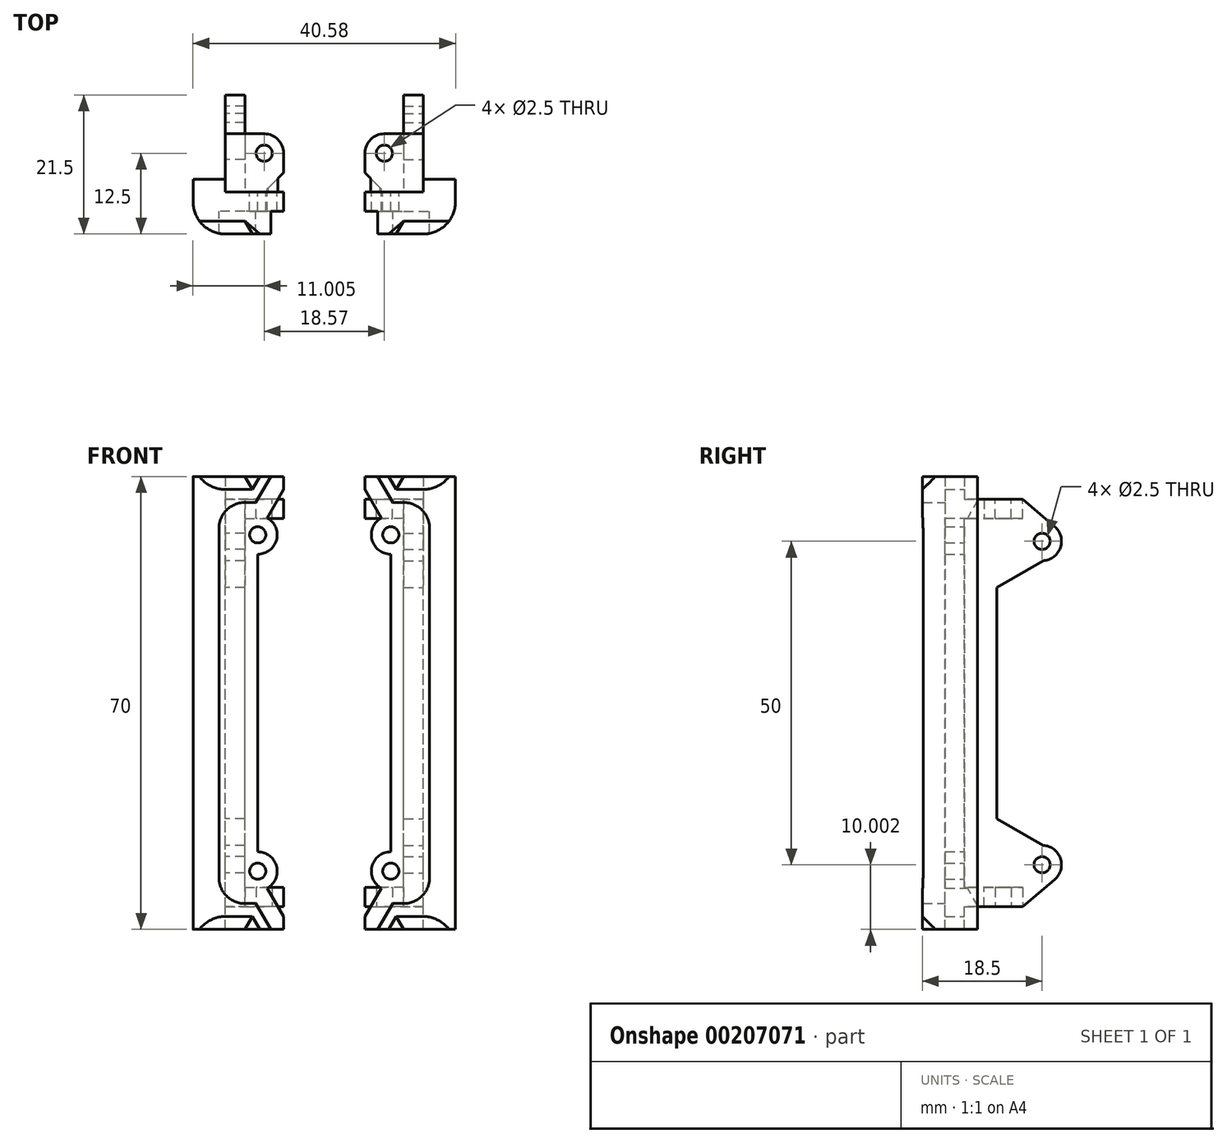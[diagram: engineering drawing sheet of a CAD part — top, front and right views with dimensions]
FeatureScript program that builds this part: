
annotation { "Feature Type Name" : "Feature", "Feature Type Description" : "" }
export const myFeature = defineFeature(function(context is Context, id is Id, definition is map)
    precondition{}
    {
        {
            var Q0;
            Q0=qCreatedBy(makeId("Front.planeOp"),FACE);
            var sketch = newSketch(context, id + "F0", { "sketchPlane" : qUnion([Q0])});
            skLineSegment(sketch, "E0", {"start": v(8.29, 4.8) * mm, "end": v(20.29, 4.8) * mm});
            skLineSegment(sketch, "E1", {"start": v(20.29, 4.8) * mm, "end": v(20.29, 13.8) * mm});
            skLineSegment(sketch, "E2", {"start": v(20.29, 13.8) * mm, "end": v(16.29, 13.8) * mm});
            skLineSegment(sketch, "E3", {"start": v(10.6, 4.8) * mm, "end": v(10.6, 8.8) * mm, "construction": true});
            skLineSegment(sketch, "E4", {"start": v(8.29, 4.8) * mm, "end": v(10.6, 8.8) * mm});
            skLineSegment(sketch, "E5", {"start": v(10.6, 8.8) * mm, "end": v(12.29, 8.8) * mm});
            skLineSegment(sketch, "E6", {"start": v(16.29, 12.8) * mm, "end": v(16.29, 13.8) * mm});
            skArc(sketch, "E7.filletArc", {"start": v(12.29, 8.8) * mm, "mid": v(15.11, 9.97) * mm, "end": v(16.29, 12.8) * mm});
            skLineSegment(sketch, "E8", {"start": v(9.19, 6.36) * mm, "end": v(12.65, 4.36) * mm, "construction": true});
            skLineSegment(sketch, "E9", {"start": v(12.29, 4.8) * mm, "end": v(15.79, 4.8) * mm});
            skLineSegment(sketch, "E10", {"start": v(20.29, 9.3) * mm, "end": v(20.29, 13.8) * mm});
            skPoint(sketch, "E11.visualSharp", {"position": v(20.29, 4.8) * mm});
            skLineSegment(sketch, "E12", {"start": v(8.29, 4.8) * mm, "end": v(6.29, 4.8) * mm});
            skLineSegment(sketch, "E13", {"start": v(6.29, 4.8) * mm, "end": v(6.29, 6.8) * mm});
            skLineSegment(sketch, "E14", {"start": v(6.29, 6.8) * mm, "end": v(8.6, 10.8) * mm});
            skLineSegment(sketch, "E15", {"start": v(16.29, 13.8) * mm, "end": v(14.29, 13.8) * mm});
            skLineSegment(sketch, "E16", {"start": v(14.29, 13.8) * mm, "end": v(10.29, 13.8) * mm, "construction": true});
            skCircle(sketch, "E17", {"center": v(10.29, 13.8) * mm, "radius": 1.25 * mm});
            skCircle(sketch, "E18", {"center": v(10.29, 13.8) * mm, "radius": 3 * mm});
            skLineSegment(sketch, "E19", {"start": v(8.6, 10.8) * mm, "end": v(8.82, 11.19) * mm});
            skLineSegment(sketch, "E20", {"start": v(10.29, 13.8) * mm, "end": v(10.29, 16.8) * mm, "construction": true});
            skLineSegment(sketch, "E21", {"start": v(10.29, 16.8) * mm, "end": v(20.29, 16.8) * mm});
            skLineSegment(sketch, "E22", {"start": v(20.29, 16.8) * mm, "end": v(20.29, 13.8) * mm});
            skLineSegment(sketch, "E23", {"start": v(20.29, 13.8) * mm, "end": v(20.29, 16.8) * mm});
            skLineSegment(sketch, "E24", {"start": v(16.29, 13.8) * mm, "end": v(16.29, 16.8) * mm});
            skLineSegment(sketch, "E25", {"start": v(12.29, 8.8) * mm, "end": v(12.29, 4.8) * mm});
            skSolve(sketch);
        }
        {
            var Q0;
            {var subQ0=sQuery(id+"F0.wireOp",EDGE,"E4");Q0=makeQuery(id+"F0.imprint","IMPRINT",FACE,{"disambiguationData":[TD([[makeQuery(id+"F0.imprint","IMPRINT",EDGE,{"derivedFrom":subQ0}),-1.0]])]});}
            var Q1;
            {var subQ0=sQuery(id+"F0.wireOp",EDGE,"E1");Q1=makeQuery(id+"F0.imprint","IMPRINT",FACE,{"disambiguationData":[TD([[makeQuery(id+"F0.imprint","IMPRINT",EDGE,{"derivedFrom":subQ0}),1.0]])]});}
            var Q2;
            Q2=makeQuery(id+"F0.imprint","IMPRINT",FACE,{"disambiguationData":[TD([[makeQuery(id+"F0.imprint","IMPRINT",EDGE,{"derivedFrom":sQuery(id+"F0.wireOp",EDGE,"E2")}),1.0]])]});
            var Q3;
            Q3=makeQuery(id+"F0.imprint","IMPRINT",FACE,{"disambiguationData":[TD([[makeQuery(id+"F0.imprint","IMPRINT",EDGE,{"derivedFrom":sQuery(id+"F0.wireOp",EDGE,"E2")}),-1.0]])]});
            extrude(context, id + "F1", {"entities" : qUnion([Q0, Q1, Q2, Q3]), "depth" : 6.5 * mm});
        }
        {
            var Q0;
            Q0 = qSketchRegion(id + "F0", true);
            extrude(context, id + "F2", {"entities" : qUnion([Q0]), "operationType" : NewBodyOperationType.ADD, "depth" : 3 * mm});
        }
        {
            var Q0;
            {var subQ0=sQuery(id+"F0.wireOp",EDGE,"E21");Q0=makeQuery(id+"F2.boolean.opBoolean","MERGE",FACE,{"derivedFrom":[makeQuery(id+"F1.opExtrude","SWEPT_FACE",FACE,{"disambiguationData":[OSD([subQ0])]}),makeQuery(id+"F2.opExtrude","SWEPT_FACE",FACE,{"disambiguationData":[OSD([subQ0])]})]});}
            var sketch = newSketch(context, id + "F3", { "sketchPlane" : qUnion([Q0])});
            skLineSegment(sketch, "E26", {"start": v(20.29, 0) * mm, "end": v(12.29, 0) * mm});
            skLineSegment(sketch, "E27", {"start": v(20.29, 0) * mm, "end": v(20.29, 2) * mm});
            skLineSegment(sketch, "E28", {"start": v(20.29, 2) * mm, "end": v(15.29, 2) * mm});
            skLineSegment(sketch, "E29", {"start": v(15.29, 2) * mm, "end": v(15.29, 5) * mm});
            skLineSegment(sketch, "E30", {"start": v(15.29, 5) * mm, "end": v(12.29, 5) * mm});
            skLineSegment(sketch, "E31", {"start": v(12.29, 5) * mm, "end": v(12.29, 0) * mm});
            skLineSegment(sketch, "E32", {"start": v(12.29, 0) * mm, "end": v(12.29, -3) * mm});
            skLineSegment(sketch, "E33", {"start": v(12.29, -3) * mm, "end": v(16.29, -3) * mm});
            skLineSegment(sketch, "E34", {"start": v(16.29, -3) * mm, "end": v(16.29, -6.5) * mm});
            skLineSegment(sketch, "E35", {"start": v(15.29, 2) * mm, "end": v(15.29, 0) * mm});
            skLineSegment(sketch, "E36", {"start": v(16.29, -6.5) * mm, "end": v(20.29, -6.5) * mm});
            skLineSegment(sketch, "E37", {"start": v(20.29, -6.5) * mm, "end": v(20.29, 0) * mm});
            skSolve(sketch);
        }
        {
            var Q0;
            Q0=makeQuery(id+"F3.imprint","IMPRINT",FACE,{"disambiguationData":[TD([[makeQuery(id+"F3.imprint","IMPRINT",EDGE,{"derivedFrom":sQuery(id+"F3.wireOp",EDGE,"E29")}),1.0]])]});
            extrude(context, id + "F4", {"entities" : qUnion([Q0]), "operationType" : NewBodyOperationType.ADD, "oppositeDirection" : true, "depth" : 8.5 * mm});
        }
        {
            var Q0;
            {var subQ0=sQuery(id+"F3.wireOp",EDGE,"E27");Q0=makeQuery(id+"F3.imprint","IMPRINT",FACE,{"disambiguationData":[TD([[makeQuery(id+"F3.imprint","IMPRINT",EDGE,{"derivedFrom":subQ0}),1.0]])]});}
            extrude(context, id + "F5", {"entities" : qUnion([Q0]), "operationType" : NewBodyOperationType.ADD, "oppositeDirection" : true, "depth" : 12 * mm});
        }
        {
            var Q0;
            Q0=makeQuery(id+"F1.opExtrude","CAP_FACE",FACE,{"disambiguationData":[OSD([sQuery(id+"F0.wireOp",EDGE,"E0"),sQuery(id+"F0.wireOp",EDGE,"E1"),sQuery(id+"F0.wireOp",EDGE,"E4"),sQuery(id+"F0.wireOp",EDGE,"E5"),sQuery(id+"F0.wireOp",EDGE,"E6"),sQuery(id+"F0.wireOp",EDGE,"E7.filletArc"),sQuery(id+"F0.wireOp",EDGE,"E9"),sQuery(id+"F0.wireOp",EDGE,"E10"),sQuery(id+"F0.wireOp",EDGE,"E21"),sQuery(id+"F0.wireOp",EDGE,"E23"),sQuery(id+"F0.wireOp",EDGE,"E24")])],"isStart":false});
            var sketch = newSketch(context, id + "F6", { "sketchPlane" : qUnion([Q0])});
            skLineSegment(sketch, "E38", {"start": v(8.29, 4.8) * mm, "end": v(12.29, 4.8) * mm});
            skLineSegment(sketch, "E39", {"start": v(8.29, 4.8) * mm, "end": v(9.79, 7.4) * mm});
            skLineSegment(sketch, "E40", {"start": v(9.79, 7.4) * mm, "end": v(13.79, 7.4) * mm});
            skLineSegment(sketch, "E41", {"start": v(13.79, 7.4) * mm, "end": v(12.29, 4.8) * mm});
            skSolve(sketch);
        }
        {
            var Q0;
            Q0=makeQuery(id+"F1.opExtrude","CAP_EDGE",EDGE,{"disambiguationData":[OSD([sQuery(id+"F0.wireOp",EDGE,"E0"),sQuery(id+"F0.wireOp",EDGE,"E9")])],"isStart":false});
            chamfer(context, id + "F7", {"entities" : qUnion([Q0]), "width" : 2 * mm, "tangentPropagation" : true});
        }
        {
            var Q0;
            Q0=makeQuery(id+"F6.imprint","IMPRINT",FACE,{"disambiguationData":[TD([[makeQuery(id+"F6.imprint","IMPRINT",EDGE,{"derivedFrom":sQuery(id+"F6.wireOp",EDGE,"E38")}),1.0]])]});
            extrude(context, id + "F8", {"entities" : qUnion([Q0]), "operationType" : NewBodyOperationType.ADD, "oppositeDirection" : true, "depth" : 3 * mm});
        }
        {
            var Q0;
            Q0=makeQuery(id+"F8.opExtrude","CAP_EDGE",EDGE,{"disambiguationData":[OSD([sQuery(id+"F6.wireOp",EDGE,"E41")])],"isStart":true});
            chamfer(context, id + "F9", {"entities" : qUnion([Q0]), "width" : 2 * mm, "tangentPropagation" : true});
        }
        {
            var Q0;
            Q0=makeQuery(id+"F4.opExtrude","CAP_FACE",FACE,{"disambiguationData":[OSD([sQuery(id+"F3.wireOp",EDGE,"E26"),sQuery(id+"F3.wireOp",EDGE,"E29"),sQuery(id+"F3.wireOp",EDGE,"E30"),sQuery(id+"F3.wireOp",EDGE,"E31"),sQuery(id+"F3.wireOp",EDGE,"E35")])],"isStart":false});
            var sketch = newSketch(context, id + "F10", { "sketchPlane" : qUnion([Q0])});
            skLineSegment(sketch, "E42", {"start": v(15.29, 0) * mm, "end": v(15.29, -6) * mm, "construction": true});
            skLineSegment(sketch, "E43", {"start": v(15.29, -6) * mm, "end": v(9.29, -6) * mm, "construction": true});
            skCircle(sketch, "E44", {"center": v(9.29, -6) * mm, "radius": 1.25 * mm});
            skCircle(sketch, "E45", {"center": v(9.29, -6) * mm, "radius": 3 * mm});
            skLineSegment(sketch, "E46", {"start": v(9.29, -6) * mm, "end": v(15.29, 0) * mm, "construction": true});
            skLineSegment(sketch, "E47", {"start": v(9.29, -6) * mm, "end": v(7.16, -3.88) * mm, "construction": true});
            skLineSegment(sketch, "E48", {"start": v(9.29, -6) * mm, "end": v(11.4, -8.12) * mm, "construction": true});
            skLineSegment(sketch, "E49", {"start": v(15.29, -5) * mm, "end": v(15.29, -9) * mm});
            skLineSegment(sketch, "E50", {"start": v(15.29, -9) * mm, "end": v(9.29, -9) * mm});
            skLineSegment(sketch, "E51", {"start": v(15.29, 0) * mm, "end": v(6.29, 0) * mm});
            skLineSegment(sketch, "E52", {"start": v(6.29, 0) * mm, "end": v(6.29, -6) * mm});
            skSolve(sketch);
        }
        {
            var Q0;
            Q0 = qSketchRegion(id + "F10", true);
            var Q1;
            Q1=makeQuery(id+"F10.imprint","IMPRINT",FACE,{"disambiguationData":[TD([[makeQuery(id+"F10.imprint","IMPRINT",EDGE,{"derivedFrom":sQuery(id+"F10.wireOp",EDGE,"E49")}),-1.0]])]});
            extrude(context, id + "F11", {"entities" : qUnion([Q0, Q1]), "operationType" : NewBodyOperationType.ADD, "oppositeDirection" : true, "depth" : 3 * mm});
        }
        {
            var Q0;
            Q0=makeQuery(id+"F11.opExtrude","SWEPT_EDGE",EDGE,{"disambiguationData":[OSD([sQuery(id+"F10.wireOp",EDGE,"E51"),sQuery(id+"F10.wireOp",EDGE,"E52")])]});
            chamfer(context, id + "F12", {"entities" : qUnion([Q0]), "width" : 3 * mm, "tangentPropagation" : true});
        }
        {
            var Q0;
            {var subQ0=sQuery(id+"F3.wireOp",EDGE,"E35");var subQ1=sQuery(id+"F3.wireOp",EDGE,"E26");var subQ2=sQuery(id+"F0.wireOp",EDGE,"E21");Q0=makeQuery(id+"F5.boolean.opBoolean","MERGE",FACE,{"derivedFrom":[makeQuery(id+"F4.boolean.opBoolean","MERGE",FACE,{"derivedFrom":[makeQuery(id+"F2.boolean.opBoolean","MERGE",FACE,{"derivedFrom":[makeQuery(id+"F1.opExtrude","SWEPT_FACE",FACE,{"disambiguationData":[OSD([subQ2])]}),makeQuery(id+"F2.opExtrude","SWEPT_FACE",FACE,{"disambiguationData":[OSD([subQ2])]})]}),makeQuery(id+"F4.opExtrude","CAP_FACE",FACE,{"disambiguationData":[OSD([subQ1,sQuery(id+"F3.wireOp",EDGE,"E29"),sQuery(id+"F3.wireOp",EDGE,"E30"),sQuery(id+"F3.wireOp",EDGE,"E31"),subQ0])],"isStart":true})]}),makeQuery(id+"F5.opExtrude","CAP_FACE",FACE,{"disambiguationData":[OSD([subQ1,sQuery(id+"F3.wireOp",EDGE,"E27"),sQuery(id+"F3.wireOp",EDGE,"E28"),subQ0])],"isStart":true})]});}
            extrude(context, id + "F13", {"entities" : qUnion([Q0]), "operationType" : NewBodyOperationType.ADD, "depth" : 23 * mm});
        }
        {
            var Q0;
            {var subQ0=sQuery(id+"F3.wireOp",EDGE,"E35");var subQ1=sQuery(id+"F3.wireOp",EDGE,"E29");Q0=makeQuery(id+"F13.boolean.opBoolean","MERGE",FACE,{"derivedFrom":[makeQuery(id+"F11.boolean.opBoolean","MERGE",FACE,{"derivedFrom":[makeQuery(id+"F4.opExtrude","SWEPT_FACE",FACE,{"disambiguationData":[OSD([subQ1,subQ0])]}),makeQuery(id+"F11.opExtrude","SWEPT_FACE",FACE,{"disambiguationData":[OSD([sQuery(id+"F10.wireOp",EDGE,"E49")])]})]}),makeQuery(id+"F13.opExtrude","SWEPT_FACE",FACE,{"disambiguationData":[OSD([subQ1,subQ0])]})]});}
            var sketch = newSketch(context, id + "F14", { "sketchPlane" : qUnion([Q0])});
            skLineSegment(sketch, "E53", {"start": v(5, 11.3) * mm, "end": v(5, 14.8) * mm});
            skCircle(sketch, "E54", {"center": v(12, 14.8) * mm, "radius": 1.25 * mm});
            skCircle(sketch, "E55", {"center": v(12, 14.8) * mm, "radius": 3 * mm});
            skLineSegment(sketch, "E56", {"start": v(12.15, 17.8) * mm, "end": v(5, 21.93) * mm});
            skLineSegment(sketch, "E57", {"start": v(5, 21.93) * mm, "end": v(5, 14.8) * mm});
            skLineSegment(sketch, "E58", {"start": v(12, 14.8) * mm, "end": v(5, 14.8) * mm, "construction": true});
            skLineSegment(sketch, "E59", {"start": v(9, 8.3) * mm, "end": v(13.95, 12.52) * mm});
            skSolve(sketch);
        }
        {
            var Q0;
            Q0=makeQuery(id+"F14.imprint","IMPRINT",FACE,{"disambiguationData":[TD([[makeQuery(id+"F14.imprint","IMPRINT",EDGE,{"derivedFrom":sQuery(id+"F14.wireOp",EDGE,"E53")}),-1.0]])]});
            var Q1;
            Q1=makeQuery(id+"F14.imprint","IMPRINT",FACE,{"disambiguationData":[TD([[makeQuery(id+"F14.imprint","IMPRINT",EDGE,{"derivedFrom":sQuery(id+"F14.wireOp",EDGE,"E54")}),-1.0]])]});
            var Q2;
            {var subQ0=sQuery(id+"F14.wireOp",EDGE,"E59");Q2=makeQuery(id+"F14.imprint","IMPRINT",FACE,{"disambiguationData":[TD([[makeQuery(id+"F14.imprint","IMPRINT",EDGE,{"derivedFrom":subQ0}),1.0]])]});}
            extrude(context, id + "F15", {"entities" : qUnion([Q0, Q1, Q2]), "operationType" : NewBodyOperationType.ADD, "oppositeDirection" : true, "depth" : 3 * mm});
        }
        {
            var Q0;
            Q0=makeQuery(id+"F1.opExtrude","SWEPT_BODY",BODY,{"disambiguationData":[OSD([sQuery(id+"F0.wireOp",EDGE,"E0"),sQuery(id+"F0.wireOp",EDGE,"E1"),sQuery(id+"F0.wireOp",EDGE,"E4"),sQuery(id+"F0.wireOp",EDGE,"E5"),sQuery(id+"F0.wireOp",EDGE,"E6"),sQuery(id+"F0.wireOp",EDGE,"E7.filletArc"),sQuery(id+"F0.wireOp",EDGE,"E9"),sQuery(id+"F0.wireOp",EDGE,"E10"),sQuery(id+"F0.wireOp",EDGE,"E21"),sQuery(id+"F0.wireOp",EDGE,"E23"),sQuery(id+"F0.wireOp",EDGE,"E24")])]});
            var Q1;
            Q1=makeQuery(id+"F13.opExtrude","CAP_FACE",FACE,{"disambiguationData":[OSD([sQuery(id+"F0.wireOp",EDGE,"E21"),sQuery(id+"F3.wireOp",EDGE,"E26"),sQuery(id+"F3.wireOp",EDGE,"E27"),sQuery(id+"F3.wireOp",EDGE,"E28"),sQuery(id+"F3.wireOp",EDGE,"E29"),sQuery(id+"F3.wireOp",EDGE,"E30"),sQuery(id+"F3.wireOp",EDGE,"E31"),sQuery(id+"F3.wireOp",EDGE,"E35")])],"isStart":false});
            mirror(context, id + "F16", {"operationType" : NewBodyOperationType.ADD, "entities" : qUnion([Q0]), "mirrorPlane" : qUnion([Q1])});
        }
        {
            var Q0;
            {var subQ0=sQuery(id+"F0.wireOp",EDGE,"E23");var subQ1=makeQuery(id+"F13.boolean.opBoolean","MERGE",EDGE,{"derivedFrom":[makeQuery(id+"F1.opExtrude","CAP_EDGE",EDGE,{"disambiguationData":[OSD([sQuery(id+"F0.wireOp",EDGE,"E1"),sQuery(id+"F0.wireOp",EDGE,"E10"),subQ0])],"isStart":false}),makeQuery(id+"F13.opExtrude","SWEPT_EDGE",EDGE,{"disambiguationData":[OSD([sQuery(id+"F0.wireOp",EDGE,"E21"),subQ0])]})]});Q0=makeQuery(id+"F16.boolean.opBoolean","MERGE",EDGE,{"derivedFrom":[subQ1,makeQuery(id+"F16.opPattern","COPY",EDGE,{"derivedFrom":subQ1,"instanceName":"1"})]});}
            fillet(context, id + "F17", {"entities" : qUnion([Q0]), "radius" : 5 * mm, "tangentPropagation" : true, "allowEdgeOverflow" : false});
        }
        {
            var Q0;
            Q0=makeQuery(id+"F1.opExtrude","SWEPT_BODY",BODY,{"disambiguationData":[OSD([sQuery(id+"F0.wireOp",EDGE,"E0"),sQuery(id+"F0.wireOp",EDGE,"E1"),sQuery(id+"F0.wireOp",EDGE,"E4"),sQuery(id+"F0.wireOp",EDGE,"E5"),sQuery(id+"F0.wireOp",EDGE,"E6"),sQuery(id+"F0.wireOp",EDGE,"E7.filletArc"),sQuery(id+"F0.wireOp",EDGE,"E9"),sQuery(id+"F0.wireOp",EDGE,"E10"),sQuery(id+"F0.wireOp",EDGE,"E21"),sQuery(id+"F0.wireOp",EDGE,"E23"),sQuery(id+"F0.wireOp",EDGE,"E24")])]});
            var Q1;
            Q1=qCreatedBy(makeId("Right.planeOp"),FACE);
            mirror(context, id + "F18", {"entities" : qUnion([Q0]), "mirrorPlane" : qUnion([Q1])});
        }
    });
